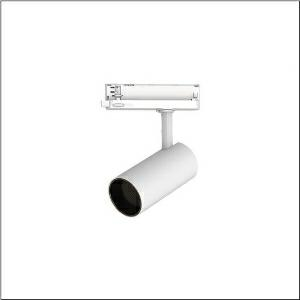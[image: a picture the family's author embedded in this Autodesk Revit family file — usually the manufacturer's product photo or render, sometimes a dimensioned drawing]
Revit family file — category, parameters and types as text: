
# Revit family: spot_31_slim_51sf117fb3b
name_source: partatom
category: Lighting Fixtures
units: mm (PartAtom-declared; Revit-internal decimal feet)

## family parameters
Cut with Voids When Loaded = No
Host = Face
Light Source = No
Part Type = Normal
Room Calculation Point = No
Round Connector Dimension = Use Diameter
Shared = No

## types (1)
- Spot 31 Slim (1 x LED, 2180 lm, 23.7 W, 3000K)
    Apparent Load = 24 VA
    CIE Flux Codes = 99 100 100 100 100
    Color Rendering = 90
    Color Temperature = 3000K
    Default Elevation = 1800 mm
    Description = Spot 31 Slim, directional spotlight, light control with reflector, of aluminium, anti glare with honeycomb louvre, LED rated luminous flux: 2.200lm, light colour: 930, control gear: ECG, with 3-phase adapter, mains connection: 220..240V, AC, 50/60Hz, housing, of aluminium, traffic white (RAL 9016), diameter: 70mm, adapter, of plastic, protection rating (complete): IP20, insulation class (complete): insulation class I (protective earthing), certification: CE, impact resistance: IK02, packaging unit: 1 piece
    Height = 210 mm
    Lamp = 1 x LED
    Lamp Light Flux = 2180 lm
    Lamp Power = 23.7 W
    Lamp count = 1
    Length = 70 mm
    Luminous efficacy = 92 lm/W
    Manufacturer = Siteco
    ModVariant = No
    Model = 51SF117FB3B
    Mounting Place = Ceiling
    Mounting Type = Pendant
    Number of Poles = 1
    OnlyDefault = Yes
    Power Factor = 1
    Product Name = Spot 31 Slim
    Product group = directional spotlight
    ProductGroupID = 905
    Protection Class = Protection class I
    Protection Degree = IP 20
    RLX_Detail_Level = 1
    RLX_Emergency_Light_Flux = 0 lm
    RLX_Emergency_Type = 0
    RLX_Emergency_Type_DB = No
    RlxData = <blob elided: 14277 chars, md5=d60ab114>
    Socket = socket
    Standby Power = 0 W
    System Light Flux = 2180 lm
    System Power = 24 W
    Type Comments = Product without accessories
    Type Image = l_1228472.jpg
    URL = http://relux.com
    VarID = ---
    Voltage = 0 V
    Weight = 0.00 kg
    Width = 0 mm  [stored 0 ft]

note: [stored X ft] marks values corroborated as IEEE doubles in the binary element streams (Revit-internal decimal feet)

## geometry (parser evidence)
native form markers: Sweep x11
no freeform markers — native parametric forms only
